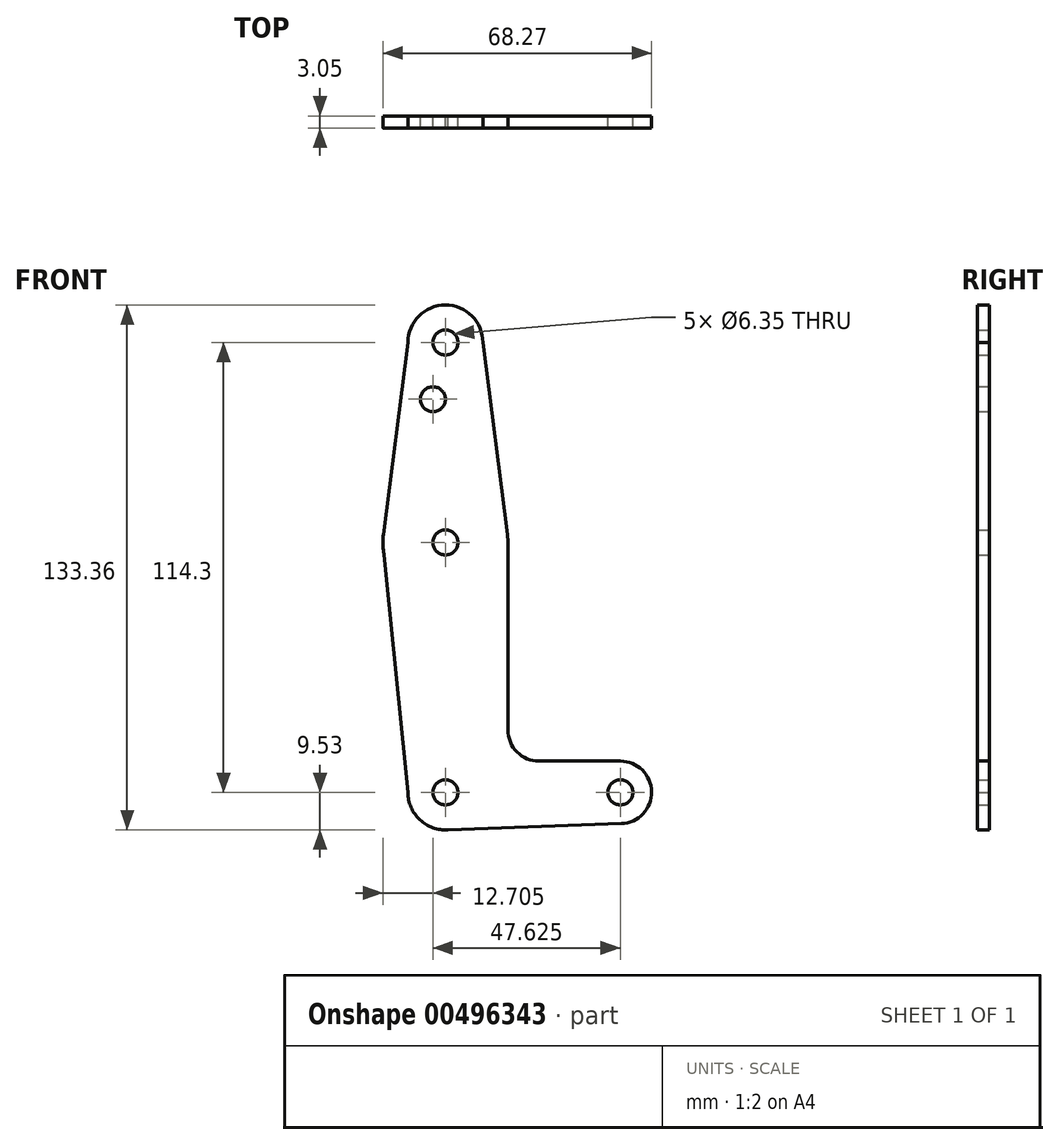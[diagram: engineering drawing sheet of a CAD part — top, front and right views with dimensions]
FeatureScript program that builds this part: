
annotation { "Feature Type Name" : "Feature", "Feature Type Description" : "" }
export const myFeature = defineFeature(function(context is Context, id is Id, definition is map)
    precondition{}
    {
        {
            var Q0;
            Q0=qCreatedBy(makeId("Front.planeOp"),FACE);
            var sketch = newSketch(context, id + "F0", { "sketchPlane" : qUnion([Q0])});
            skLineSegment(sketch, "E0", {"start": v(0, 0) * mm, "end": v(0, 63.5) * mm});
            skLineSegment(sketch, "E1", {"start": v(0, 0) * mm, "end": v(44.45, 0) * mm});
            skLineSegment(sketch, "E2", {"start": v(0, 63.5) * mm, "end": v(0, 114.3) * mm});
            skCircle(sketch, "E3", {"center": v(44.45, 0) * mm, "radius": 7.94 * mm});
            skCircle(sketch, "E4", {"center": v(0, 63.5) * mm, "radius": 15.88 * mm});
            skCircle(sketch, "E5", {"center": v(0, 0) * mm, "radius": 9.53 * mm});
            skCircle(sketch, "E6", {"center": v(0, 114.3) * mm, "radius": 9.53 * mm});
            skLineSegment(sketch, "E7", {"start": v(-9.52, 114.3) * mm, "end": v(-15.75, 65.5) * mm});
            skLineSegment(sketch, "E8", {"start": v(9.52, 114.3) * mm, "end": v(15.75, 65.5) * mm});
            skLineSegment(sketch, "E9", {"start": v(-15.88, 63.5) * mm, "end": v(-9.52, 0) * mm});
            skLineSegment(sketch, "E10", {"start": v(15.87, 63.5) * mm, "end": v(15.88, 15.89) * mm});
            skLineSegment(sketch, "E11", {"start": v(23.83, 7.94) * mm, "end": v(44.45, 7.94) * mm});
            skLineSegment(sketch, "E12", {"start": v(0, -9.53) * mm, "end": v(44.73, -7.93) * mm});
            skCircle(sketch, "E13", {"center": v(-3.18, 99.89) * mm, "radius": 3.18 * mm});
            skArc(sketch, "E14.filletArc", {"start": v(15.88, 15.89) * mm, "mid": v(18.2, 10.27) * mm, "end": v(23.83, 7.94) * mm});
            skCircle(sketch, "E15", {"center": v(0, 114.3) * mm, "radius": 3.18 * mm});
            skCircle(sketch, "E16", {"center": v(0, 63.5) * mm, "radius": 3.18 * mm});
            skCircle(sketch, "E17", {"center": v(0, 0) * mm, "radius": 3.18 * mm});
            skCircle(sketch, "E18", {"center": v(44.45, 0) * mm, "radius": 3.18 * mm});
            skSolve(sketch);
        }
        {
            var Q0;
            Q0 = qSketchRegion(id + "F0", true);
            var Q1;
            {var subQ0=sQuery(id+"F0.wireOp",EDGE,"E17");var subQ1=sQuery(id+"F0.wireOp",EDGE,"E0");var subQ2=makeQuery(id+"F0.imprint","INTERSECT",VERTEX,{"derivedFrom":[subQ1,subQ0]});Q1=makeQuery(id+"F0.imprint","IMPRINT",FACE,{"disambiguationData":[TD([[makeQuery(id+"F0.imprint","IMPRINT",EDGE,{"disambiguationData":[TD([[subQ2,-1.0]])],"derivedFrom":subQ1}),-1.0]])]});}
            extrude(context, id + "F1", {"entities" : qUnion([Q0, Q1]), "depth" : 3.05 * mm});
        }
    });
